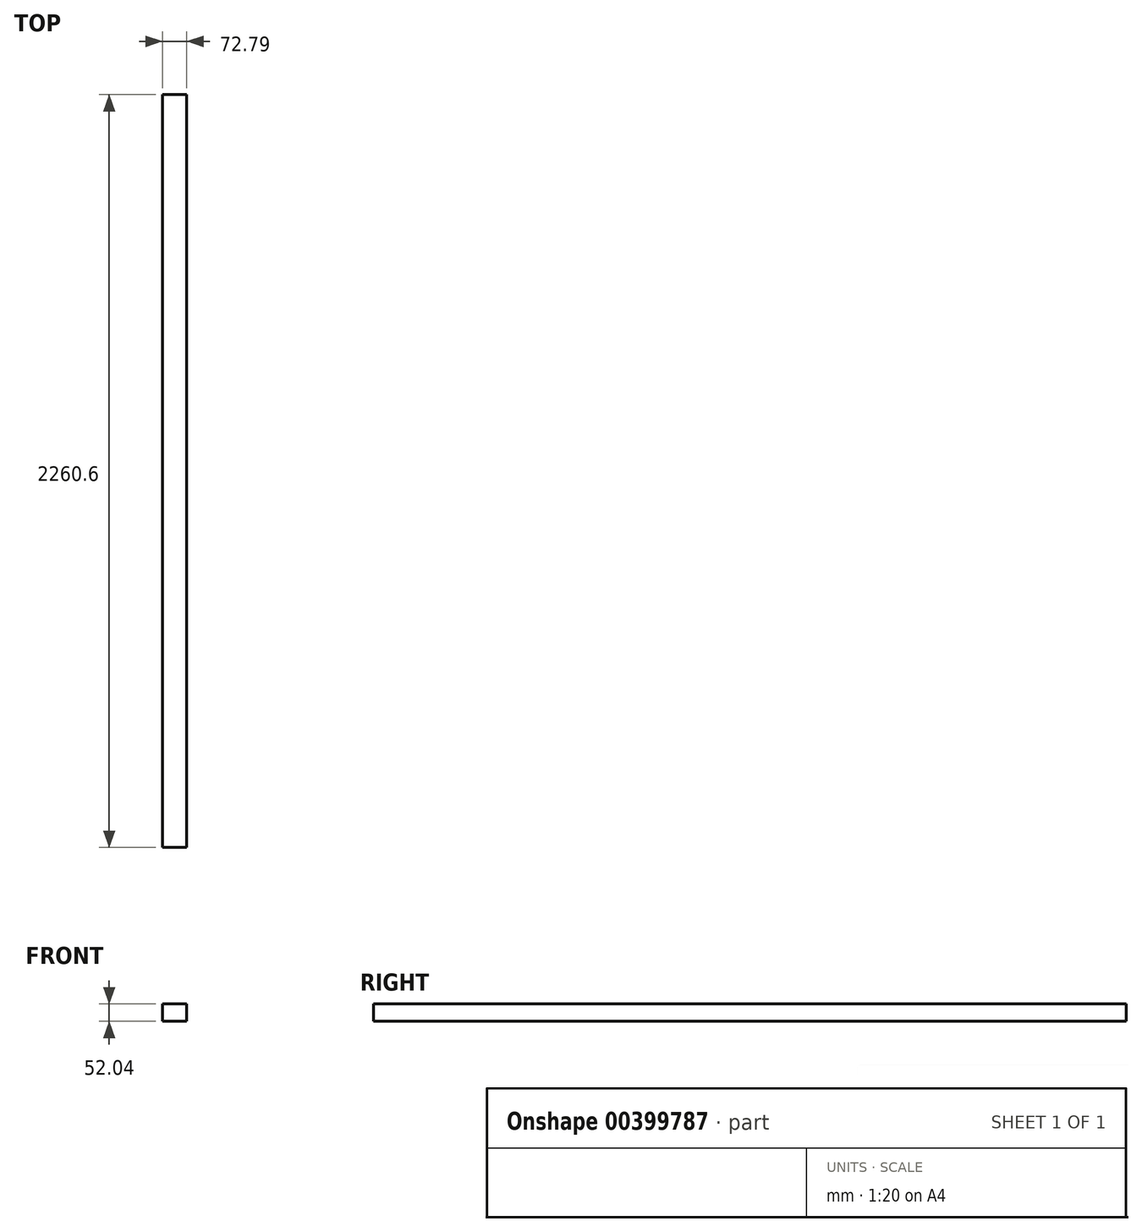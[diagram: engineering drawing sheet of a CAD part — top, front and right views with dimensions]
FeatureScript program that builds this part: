
annotation { "Feature Type Name" : "Feature", "Feature Type Description" : "" }
export const myFeature = defineFeature(function(context is Context, id is Id, definition is map)
    precondition{}
    {
        {
            var Q0;
            Q0=qCreatedBy(makeId("Front.planeOp"),FACE);
            var sketch = newSketch(context, id + "F0", { "sketchPlane" : qUnion([Q0])});
            skLineSegment(sketch, "E0", {"start": v(0, 0) * mm, "end": v(72.8, 0) * mm});
            skLineSegment(sketch, "E1", {"start": v(72.8, 0) * mm, "end": v(72.8, 52.04) * mm});
            skLineSegment(sketch, "E2", {"start": v(72.8, 52.04) * mm, "end": v(0, 52.04) * mm});
            skLineSegment(sketch, "E3", {"start": v(0, 52.04) * mm, "end": v(0, 0) * mm});
            skSolve(sketch);
        }
        {
            var Q0;
            Q0 = qSketchRegion(id + "F0", true);
            extrude(context, id + "F1", {"entities" : qUnion([Q0]), "depth" : 2260.6 * mm});
        }
    });
